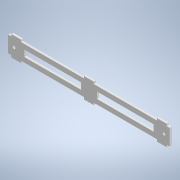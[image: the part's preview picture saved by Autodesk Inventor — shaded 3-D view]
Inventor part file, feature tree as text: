
AUTODESK INVENTOR PART (.ipt)
format: ipt  version: 2022 (Build 260153000, 153)  size: 151,040 bytes
history: native  units: mm
features: other x3, extrude x1, reference x1
ambient origin geometry x8: Origin, YZ Plane, XZ Plane, XY Plane, X Axis, Y Axis, Z Axis, Center Point
bodies: Body1 (feature_tree)
feature tree (5):
  extrude  "Extrusion4"  Depth=250.0mm
  reference  "Reference2"
  other  "<userpath>\OneDrive\Escritorio\Mini_Proyecto_Diseno\Diseno_18012\Modelo_MPD\Carril.iam"
  other  "Carril.iam"
  other  "Tope_Carril:1"
